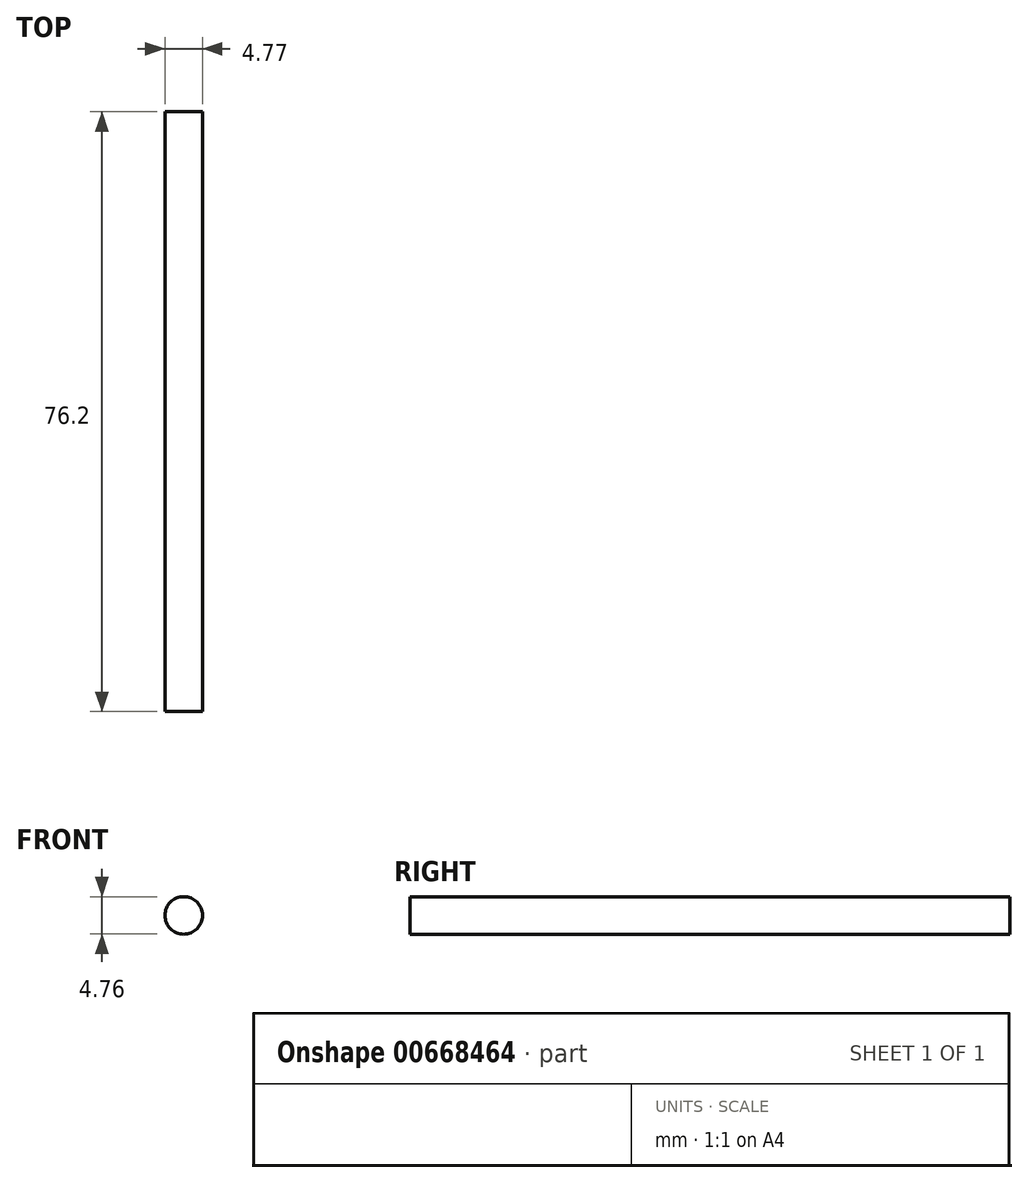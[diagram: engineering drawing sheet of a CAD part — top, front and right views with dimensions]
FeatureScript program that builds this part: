
annotation { "Feature Type Name" : "Feature", "Feature Type Description" : "" }
export const myFeature = defineFeature(function(context is Context, id is Id, definition is map)
    precondition{}
    {
        {
            var Q0;
            Q0=qCreatedBy(makeId("Front.planeOp"),FACE);
            var sketch = newSketch(context, id + "F0", { "sketchPlane" : qUnion([Q0])});
            skCircle(sketch, "E0", {"center": v(-25.67, 17.46) * mm, "radius": 2.38 * mm});
            skSolve(sketch);
        }
        {
            var Q0;
            Q0=makeQuery(id+"F0.imprint","IMPRINT",FACE,{"disambiguationData":[TD([[makeQuery(id+"F0.imprint","IMPRINT",EDGE,{"derivedFrom":sQuery(id+"F0.wireOp",EDGE,"E0")}),1.0]])]});
            extrude(context, id + "F1", {"entities" : qUnion([Q0]), "depth" : 76.2 * mm});
        }
    });
